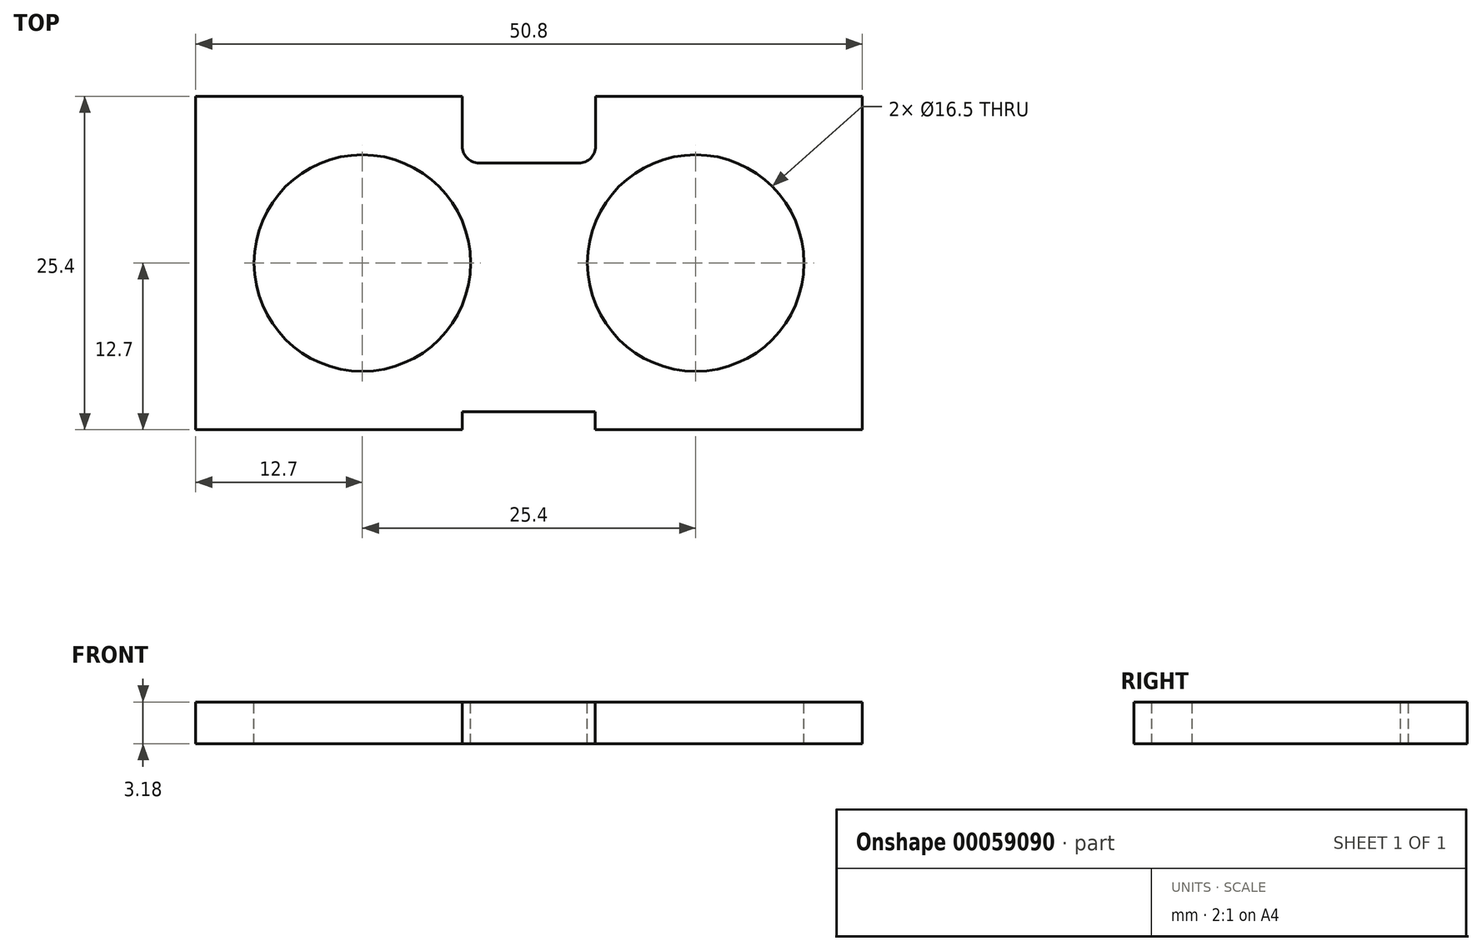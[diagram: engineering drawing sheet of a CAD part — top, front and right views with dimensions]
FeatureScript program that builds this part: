
annotation { "Feature Type Name" : "Feature", "Feature Type Description" : "" }
export const myFeature = defineFeature(function(context is Context, id is Id, definition is map)
    precondition{}
    {
        {
            var Q0;
            Q0=qCreatedBy(makeId("Top.planeOp"),FACE);
            var sketch = newSketch(context, id + "F0", { "sketchPlane" : qUnion([Q0])});
            skLineSegment(sketch, "E0.bottom", {"start": v(-25.4, 12.7) * mm, "end": v(25.4, 12.7) * mm});
            skLineSegment(sketch, "E0.top", {"start": v(-25.4, -12.7) * mm, "end": v(25.4, -12.7) * mm});
            skLineSegment(sketch, "E0.left", {"start": v(-25.4, 12.7) * mm, "end": v(-25.4, -12.7) * mm});
            skLineSegment(sketch, "E0.right", {"start": v(25.4, 12.7) * mm, "end": v(25.4, -12.7) * mm});
            skSolve(sketch);
        }
        {
            var Q0;
            Q0=makeQuery(id+"F0.imprint","IMPRINT",FACE,{"disambiguationData":[TD([[makeQuery(id+"F0.imprint","IMPRINT",EDGE,{"derivedFrom":sQuery(id+"F0.wireOp",EDGE,"E0.bottom")}),-1.0]])]});
            extrude(context, id + "F1", {"entities" : qUnion([Q0]), "depth" : 3.17 * mm});
        }
        {
            var Q0;
            Q0=makeQuery(id+"F1.opExtrude","CAP_FACE",FACE,{"disambiguationData":[OSD([sQuery(id+"F0.wireOp",EDGE,"E0.bottom"),sQuery(id+"F0.wireOp",EDGE,"E0.top"),sQuery(id+"F0.wireOp",EDGE,"E0.left"),sQuery(id+"F0.wireOp",EDGE,"E0.right")])],"isStart":false});
            var sketch = newSketch(context, id + "F2", { "sketchPlane" : qUnion([Q0])});
            skCircle(sketch, "E1", {"center": v(-12.7, 0) * mm, "radius": 8.25 * mm});
            skPoint(sketch, "E1.centerSnap0", {"position": v(-22.04, 0) * mm});
            skCircle(sketch, "E2", {"center": v(12.7, 0) * mm, "radius": 8.25 * mm});
            skSolve(sketch);
        }
        {
            var Q0;
            Q0=makeQuery(id+"F2.imprint","IMPRINT",FACE,{"disambiguationData":[TD([[makeQuery(id+"F2.imprint","IMPRINT",EDGE,{"derivedFrom":sQuery(id+"F2.wireOp",EDGE,"E1")}),1.0]])]});
            var Q1;
            Q1=makeQuery(id+"F2.imprint","IMPRINT",FACE,{"disambiguationData":[TD([[makeQuery(id+"F2.imprint","IMPRINT",EDGE,{"derivedFrom":sQuery(id+"F2.wireOp",EDGE,"E2")}),1.0]])]});
            extrude(context, id + "F3", {"entities" : qUnion([Q0, Q1]), "operationType" : NewBodyOperationType.REMOVE, "oppositeDirection" : true, "depth" : 25.4 * mm});
        }
        {
            var Q0;
            Q0=makeQuery(id+"F1.opExtrude","CAP_FACE",FACE,{"disambiguationData":[OSD([sQuery(id+"F0.wireOp",EDGE,"E0.bottom"),sQuery(id+"F0.wireOp",EDGE,"E0.top"),sQuery(id+"F0.wireOp",EDGE,"E0.left"),sQuery(id+"F0.wireOp",EDGE,"E0.right")])],"isStart":false});
            var sketch = newSketch(context, id + "F4", { "sketchPlane" : qUnion([Q0])});
            skLineSegment(sketch, "E3.bottom", {"start": v(-5.08, 17.63) * mm, "end": v(5.08, 17.63) * mm});
            skLineSegment(sketch, "E3.top", {"start": v(-5.08, 7.62) * mm, "end": v(5.08, 7.62) * mm});
            skLineSegment(sketch, "E3.left", {"start": v(-5.08, 17.63) * mm, "end": v(-5.08, 7.62) * mm});
            skLineSegment(sketch, "E3.right", {"start": v(5.08, 17.63) * mm, "end": v(5.08, 7.62) * mm});
            skLineSegment(sketch, "E4.bottom", {"start": v(-5.1, -11.32) * mm, "end": v(5.05, -11.32) * mm});
            skLineSegment(sketch, "E4.top", {"start": v(-5.1, -14.35) * mm, "end": v(5.05, -14.35) * mm});
            skLineSegment(sketch, "E4.left", {"start": v(-5.1, -11.32) * mm, "end": v(-5.1, -14.35) * mm});
            skLineSegment(sketch, "E4.right", {"start": v(5.05, -11.32) * mm, "end": v(5.05, -14.35) * mm});
            skSolve(sketch);
        }
        {
            var Q0;
            {var subQ0=sQuery(id+"F4.wireOp",EDGE,"E3.top");Q0=makeQuery(id+"F4.imprint","IMPRINT",FACE,{"disambiguationData":[TD([[makeQuery(id+"F4.imprint","IMPRINT",EDGE,{"derivedFrom":subQ0}),1.0]])]});}
            var Q1;
            {var subQ0=sQuery(id+"F4.wireOp",EDGE,"E4.bottom");Q1=makeQuery(id+"F4.imprint","IMPRINT",FACE,{"disambiguationData":[TD([[makeQuery(id+"F4.imprint","IMPRINT",EDGE,{"derivedFrom":subQ0}),-1.0]])]});}
            extrude(context, id + "F5", {"entities" : qUnion([Q0, Q1]), "operationType" : NewBodyOperationType.REMOVE, "oppositeDirection" : true, "depth" : 25.4 * mm});
        }
        {
            var Q0;
            Q0=makeQuery(id+"F5.boolean.opBoolean","COPY",EDGE,{"derivedFrom":makeQuery(id+"F5.opExtrude","SWEPT_EDGE",EDGE,{"disambiguationData":[OSD([sQuery(id+"F4.wireOp",EDGE,"E3.top"),sQuery(id+"F4.wireOp",EDGE,"E3.left")])]})});
            var Q1;
            Q1=makeQuery(id+"F5.boolean.opBoolean","COPY",EDGE,{"derivedFrom":makeQuery(id+"F5.opExtrude","SWEPT_EDGE",EDGE,{"disambiguationData":[OSD([sQuery(id+"F4.wireOp",EDGE,"E3.top"),sQuery(id+"F4.wireOp",EDGE,"E3.right")])]})});
            fillet(context, id + "F6", {"entities" : qUnion([Q0, Q1]), "radius" : 1.27 * mm, "tangentPropagation" : true, "allowEdgeOverflow" : false});
        }
    });
